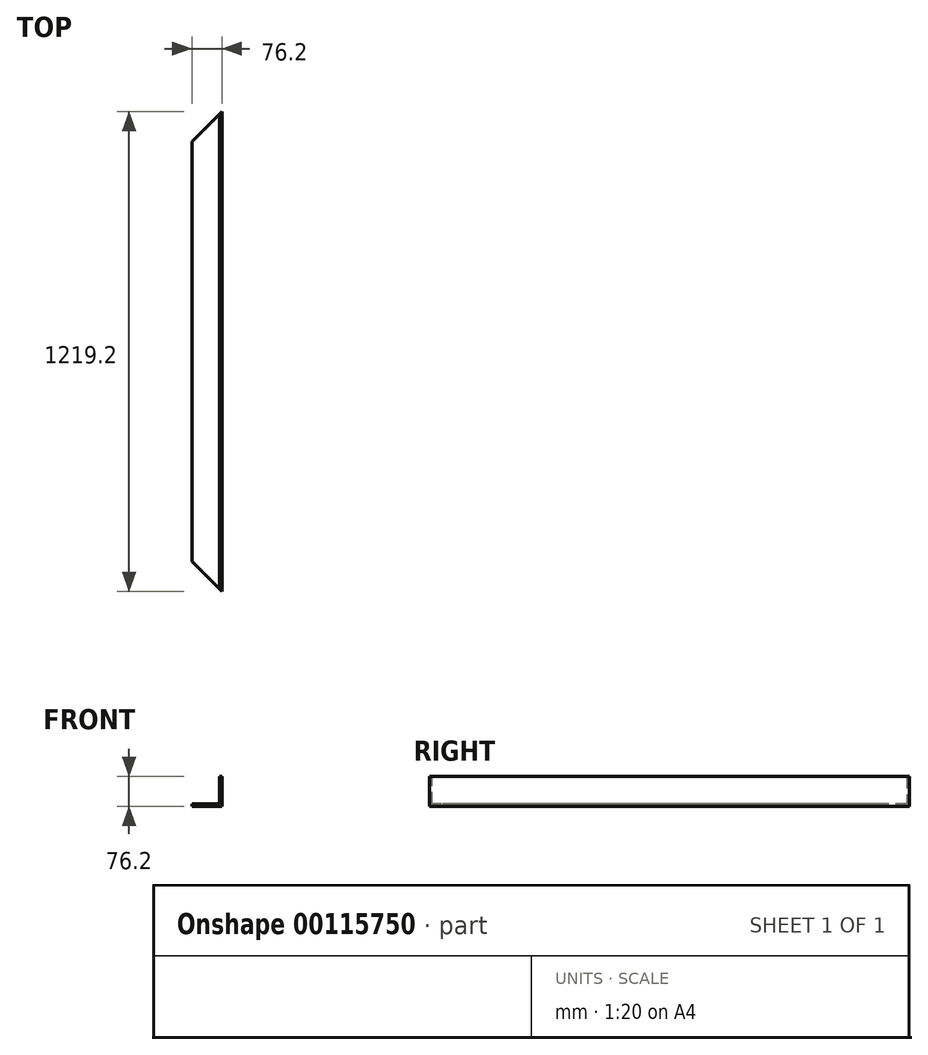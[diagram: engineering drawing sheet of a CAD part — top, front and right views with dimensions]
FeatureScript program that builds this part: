
annotation { "Feature Type Name" : "Feature", "Feature Type Description" : "" }
export const myFeature = defineFeature(function(context is Context, id is Id, definition is map)
    precondition{}
    {
        {
            var Q0;
            Q0=qCreatedBy(makeId("Front.planeOp"),FACE);
            var sketch = newSketch(context, id + "F0", { "sketchPlane" : qUnion([Q0])});
            skLineSegment(sketch, "E0", {"start": v(0, 76.2) * mm, "end": v(0, 0) * mm});
            skLineSegment(sketch, "E1", {"start": v(0, 0) * mm, "end": v(-76.2, 0) * mm});
            skLineSegment(sketch, "E2.0", {"start": v(-6.35, 6.35) * mm, "end": v(-76.2, 6.35) * mm});
            skLineSegment(sketch, "E2.1", {"start": v(-6.35, 76.2) * mm, "end": v(-6.35, 6.35) * mm});
            skLineSegment(sketch, "E3", {"start": v(-76.2, 6.35) * mm, "end": v(-76.2, 0) * mm});
            skLineSegment(sketch, "E4", {"start": v(-6.35, 76.2) * mm, "end": v(0, 76.2) * mm});
            skSolve(sketch);
        }
        {
            var Q0;
            Q0 = qSketchRegion(id + "F0", true);
            extrude(context, id + "F1", {"entities" : qUnion([Q0]), "oppositeDirection" : true, "depth" : 1219.2 * mm});
        }
        {
            var Q0;
            Q0=makeQuery(id+"F1.opExtrude","SWEPT_FACE",FACE,{"disambiguationData":[OSD([sQuery(id+"F0.wireOp",EDGE,"E4")])]});
            var sketch = newSketch(context, id + "F2", { "sketchPlane" : qUnion([Q0])});
            skLineSegment(sketch, "E5.0", {"start": v(-76.2, 1219.2) * mm, "end": v(-76.2, 1143) * mm});
            skLineSegment(sketch, "E6", {"start": v(0, 1219.2) * mm, "end": v(-76.2, 1219.2) * mm});
            skLineSegment(sketch, "E7", {"start": v(0, 0) * mm, "end": v(-76.2, 0) * mm});
            skLineSegment(sketch, "E8", {"start": v(0, 1219.2) * mm, "end": v(-76.2, 1143) * mm});
            skLineSegment(sketch, "E9", {"start": v(-76.2, 76.2) * mm, "end": v(0, 0) * mm});
            skLineSegment(sketch, "E10.trimOffspring", {"start": v(-76.2, 76.2) * mm, "end": v(-76.2, 0) * mm});
            skSolve(sketch);
        }
        {
            var Q0;
            Q0 = qSketchRegion(id + "F2", true);
            extrude(context, id + "F3", {"entities" : qUnion([Q0]), "operationType" : NewBodyOperationType.REMOVE, "oppositeDirection" : true, "depth" : 76.2 * mm});
        }
    });
